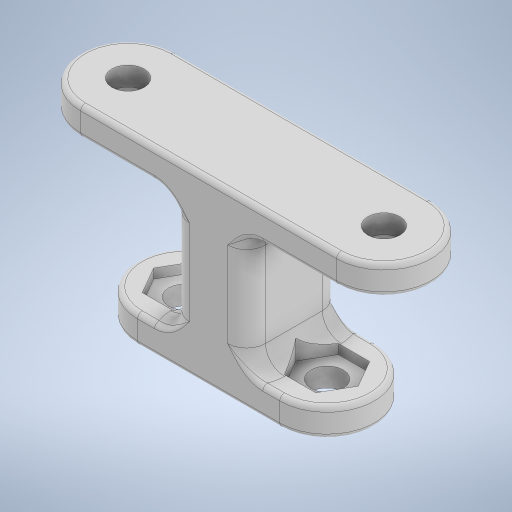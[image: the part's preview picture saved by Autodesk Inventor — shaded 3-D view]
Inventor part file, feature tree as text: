
AUTODESK INVENTOR PART (.ipt)
format: ipt  version: 2024.2 (Build 282272000, 272)  size: 423,936 bytes
history: native  units: mm
features: extrude x6, sketch x6, fillet x2
ambient origin geometry x8: Origin, YZ Plane, XZ Plane, XY Plane, X Axis, Y Axis, Z Axis, Center Point
bodies: Solid1 (feature_tree)
feature tree (14):
  extrude  "Extrusion1"  Depth=27.0mm
  extrude  "Extrusion2"  Depth=10.0mm TaperAngle=0.0deg
  extrude  "Extrusion3"  Depth=15.0mm
  extrude  "Extrusion4"  Depth=5.7mm
  extrude  "Extrusion5"  Depth=3.4mm
  extrude  "Extrusion6"  Depth=0.5mm
  fillet  "Fillet3"  Radius=1.0mm
  fillet  "Fillet2"  Radius=0.5mm
  sketch  "Sketch1"  dims[d0=3.4mm d1=27.0mm]
  sketch  "Sketch2"  dims[d2=10.0mm d3=3.0mm d4=0.0mm]
  sketch  "Sketch3"  dims[d5=13.0mm d6=0.0mm d7=15.0mm]
  sketch  "Sketch4"  dims[d8=3.0mm d9=0.0mm d10=5.7mm]
  sketch  "Sketch5"  dims[d11=1.0mm d12=0.0mm d13=3.4mm]
  sketch  "Sketch6"  dims[d14=2.0mm d15=0.0mm d16=5.1mm d17=1.0mm d18=0.0mm d20=0.5mm d22=8.0mm d23=2.0mm]
